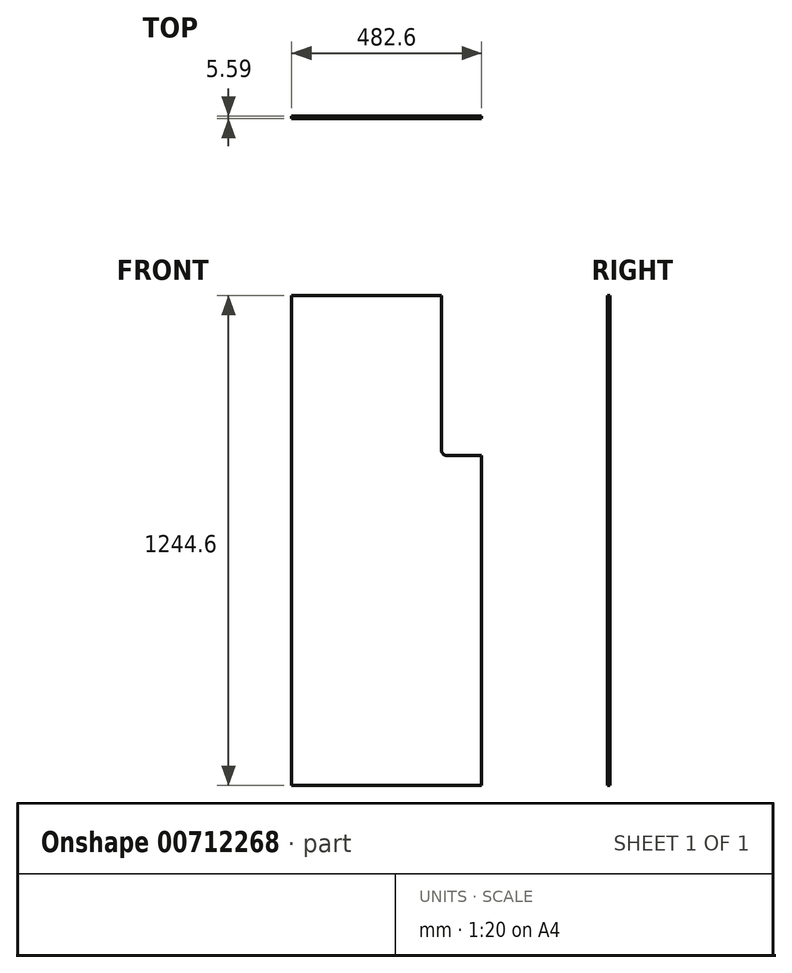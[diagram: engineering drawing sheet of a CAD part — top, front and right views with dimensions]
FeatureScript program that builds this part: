
annotation { "Feature Type Name" : "Feature", "Feature Type Description" : "" }
export const myFeature = defineFeature(function(context is Context, id is Id, definition is map)
    precondition{}
    {
        {
            var Q0;
            Q0=qCreatedBy(makeId("Front.planeOp"),FACE);
            var sketch = newSketch(context, id + "F0", { "sketchPlane" : qUnion([Q0])});
            skLineSegment(sketch, "E0.bottom", {"start": v(-413.12, 630.44) * mm, "end": v(69.48, 630.44) * mm});
            skLineSegment(sketch, "E0.top", {"start": v(-413.12, -614.16) * mm, "end": v(69.48, -614.16) * mm});
            skLineSegment(sketch, "E0.left", {"start": v(-413.12, 630.44) * mm, "end": v(-413.12, -614.16) * mm});
            skLineSegment(sketch, "E0.right", {"start": v(69.48, 630.44) * mm, "end": v(69.48, -614.16) * mm});
            skSolve(sketch);
        }
        {
            var Q0;
            Q0 = qSketchRegion(id + "F0", true);
            extrude(context, id + "F1", {"entities" : qUnion([Q0]), "depth" : 5.6 * mm, "offsetDistance" : 25.4 * mm});
        }
        {
            var Q0;
            Q0=makeQuery(id+"F1.opExtrude","CAP_FACE",FACE,{"disambiguationData":[OSD([sQuery(id+"F0.wireOp",EDGE,"E0.bottom"),sQuery(id+"F0.wireOp",EDGE,"E0.top"),sQuery(id+"F0.wireOp",EDGE,"E0.left"),sQuery(id+"F0.wireOp",EDGE,"E0.right")])],"isStart":false});
            var sketch = newSketch(context, id + "F2", { "sketchPlane" : qUnion([Q0])});
            skLineSegment(sketch, "E1.bottom", {"start": v(69.48, 630.44) * mm, "end": v(-32.12, 630.44) * mm});
            skLineSegment(sketch, "E1.top", {"start": v(69.48, 224.04) * mm, "end": v(-19.42, 224.04) * mm});
            skLineSegment(sketch, "E1.left", {"start": v(69.48, 630.44) * mm, "end": v(69.48, 224.04) * mm});
            skLineSegment(sketch, "E1.right", {"start": v(-32.12, 630.44) * mm, "end": v(-32.12, 236.74) * mm});
            skPoint(sketch, "E2.visualSharp", {"position": v(-32.12, 224.04) * mm});
            skArc(sketch, "E2.filletArc", {"start": v(-32.12, 236.74) * mm, "mid": v(-28.4, 227.76) * mm, "end": v(-19.42, 224.04) * mm});
            skSolve(sketch);
        }
        {
            var Q0;
            Q0 = qSketchRegion(id + "F2", true);
            extrude(context, id + "F3", {"entities" : qUnion([Q0]), "operationType" : NewBodyOperationType.REMOVE, "endBound" : BoundingType.THROUGH_ALL, "oppositeDirection" : true, "depth" : 25.4 * mm, "offsetDistance" : 25.4 * mm});
        }
    });
